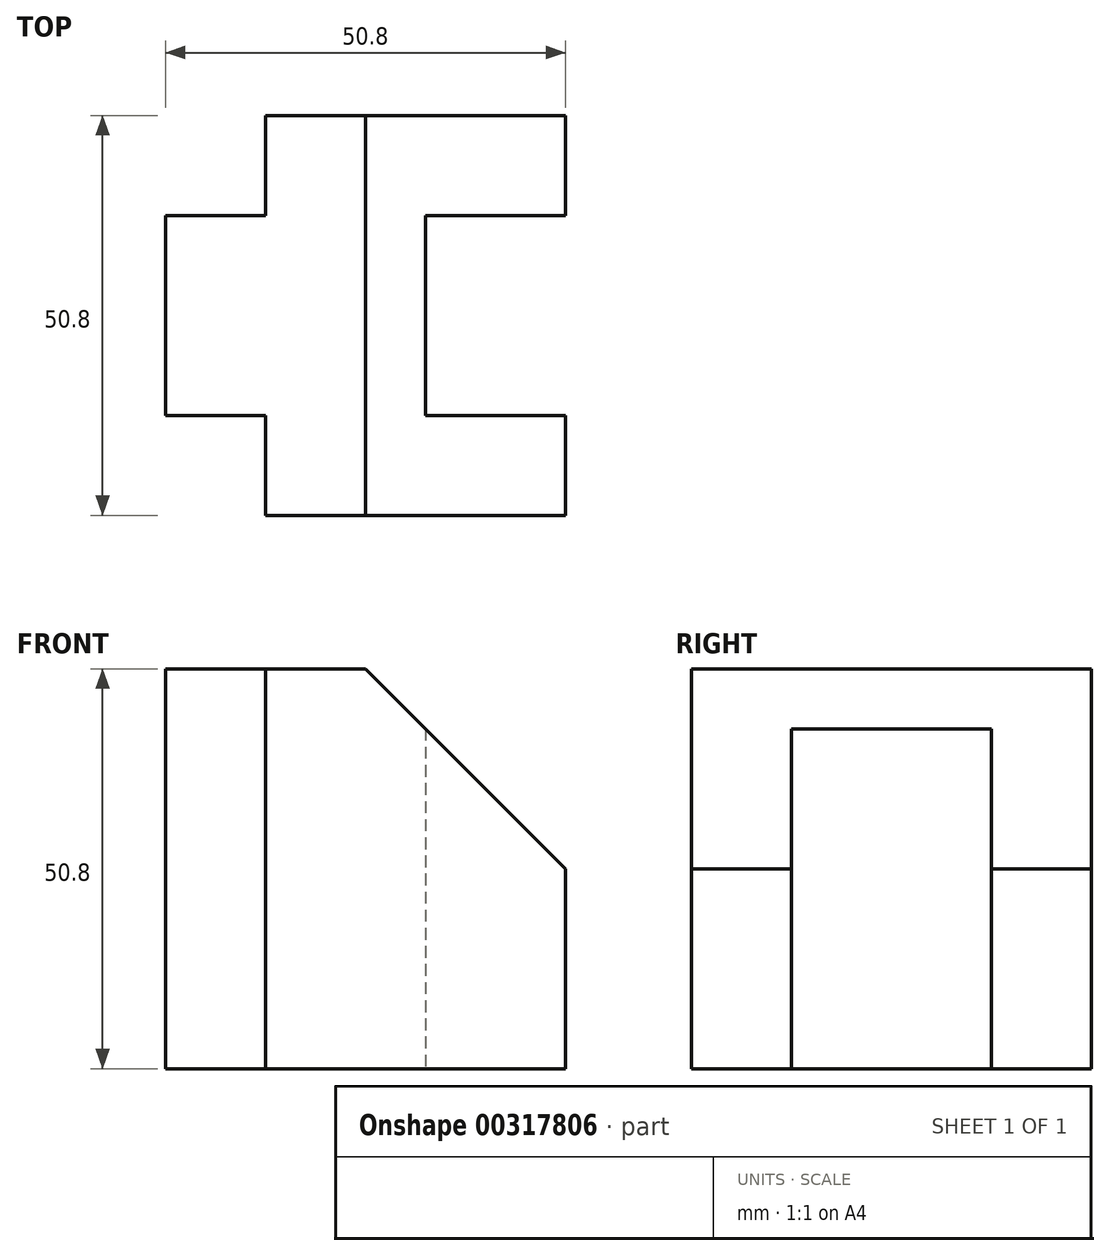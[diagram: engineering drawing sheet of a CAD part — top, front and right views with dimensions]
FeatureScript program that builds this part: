
annotation { "Feature Type Name" : "Feature", "Feature Type Description" : "" }
export const myFeature = defineFeature(function(context is Context, id is Id, definition is map)
    precondition{}
    {
        {
            var Q0;
            Q0=qCreatedBy(makeId("Front.planeOp"),FACE);
            var sketch = newSketch(context, id + "F0", { "sketchPlane" : qUnion([Q0])});
            skLineSegment(sketch, "E0", {"start": v(0, 0) * mm, "end": v(0, 50.8) * mm});
            skLineSegment(sketch, "E1", {"start": v(0, 50.8) * mm, "end": v(25.4, 50.8) * mm});
            skLineSegment(sketch, "E2", {"start": v(25.4, 50.8) * mm, "end": v(50.8, 25.4) * mm});
            skLineSegment(sketch, "E3", {"start": v(50.8, 25.4) * mm, "end": v(50.8, 0) * mm});
            skLineSegment(sketch, "E4", {"start": v(50.8, 0) * mm, "end": v(0, 0) * mm});
            skLineSegment(sketch, "E5", {"start": v(12.7, 50.8) * mm, "end": v(12.7, 0) * mm});
            skSolve(sketch);
        }
        {
            var Q0;
            Q0 = qSketchRegion(id + "F0", true);
            extrude(context, id + "F1", {"entities" : qUnion([Q0]), "depth" : 50.8 * mm});
        }
        {
            var Q0;
            Q0=makeQuery(id+"F1.opExtrude","SWEPT_FACE",FACE,{"disambiguationData":[OSD([sQuery(id+"F0.wireOp",EDGE,"E4")])]});
            var sketch = newSketch(context, id + "F2", { "sketchPlane" : qUnion([Q0])});
            skLineSegment(sketch, "E6", {"start": v(0, 38.1) * mm, "end": v(12.7, 38.1) * mm});
            skLineSegment(sketch, "E7", {"start": v(12.7, 38.1) * mm, "end": v(12.7, 50.8) * mm});
            skLineSegment(sketch, "E8", {"start": v(0, 12.7) * mm, "end": v(12.7, 12.7) * mm});
            skLineSegment(sketch, "E9", {"start": v(12.7, 12.7) * mm, "end": v(12.7, 0) * mm});
            skLineSegment(sketch, "E10", {"start": v(50.8, 38.1) * mm, "end": v(33.02, 38.1) * mm});
            skLineSegment(sketch, "E11", {"start": v(33.02, 38.1) * mm, "end": v(33.02, 12.7) * mm});
            skLineSegment(sketch, "E12", {"start": v(33.02, 12.7) * mm, "end": v(50.8, 12.7) * mm});
            skLineSegment(sketch, "E13", {"start": v(50.8, 12.7) * mm, "end": v(50.8, 38.1) * mm});
            skSolve(sketch);
        }
        {
            var Q0;
            {var subQ0=sQuery(id+"F2.wireOp",EDGE,"E6");Q0=makeQuery(id+"F2.imprint","IMPRINT",FACE,{"disambiguationData":[TD([[makeQuery(id+"F2.imprint","IMPRINT",EDGE,{"derivedFrom":subQ0}),1.0]])]});}
            var Q1;
            {var subQ0=sQuery(id+"F2.wireOp",EDGE,"E8");Q1=makeQuery(id+"F2.imprint","IMPRINT",FACE,{"disambiguationData":[TD([[makeQuery(id+"F2.imprint","IMPRINT",EDGE,{"derivedFrom":subQ0}),-1.0]])]});}
            var Q2;
            Q2=makeQuery(id+"F2.imprint","IMPRINT",FACE,{"disambiguationData":[TD([[makeQuery(id+"F2.imprint","IMPRINT",EDGE,{"derivedFrom":sQuery(id+"F2.wireOp",EDGE,"E10")}),1.0]])]});
            extrude(context, id + "F3", {"entities" : qUnion([Q0, Q1, Q2]), "operationType" : NewBodyOperationType.REMOVE, "endBound" : BoundingType.THROUGH_ALL, "oppositeDirection" : true, "depth" : 25.4 * mm});
        }
    });
